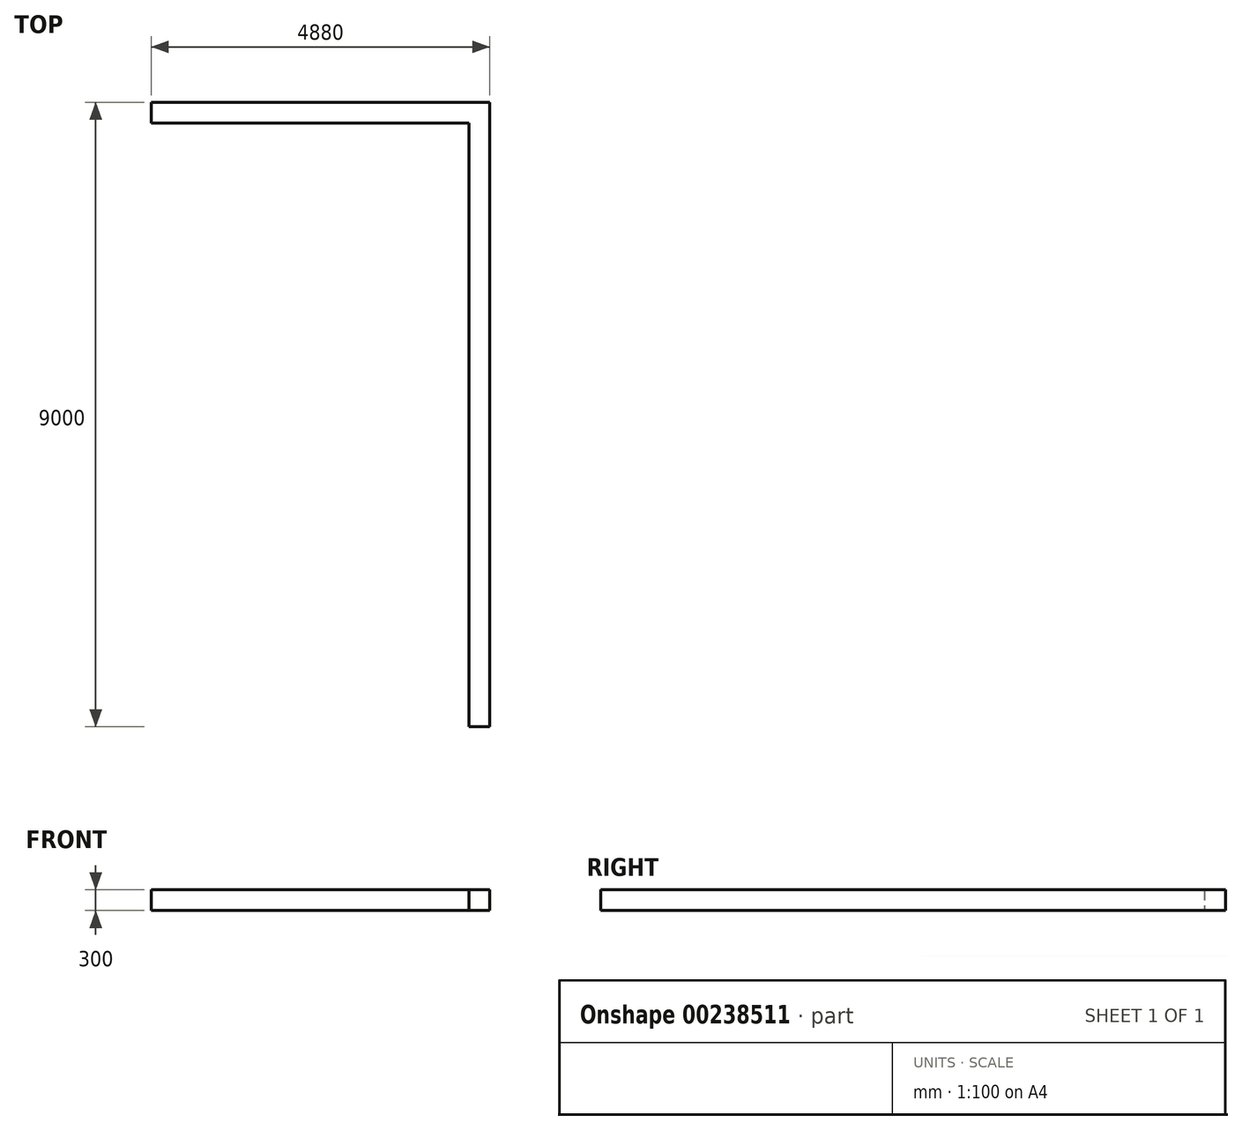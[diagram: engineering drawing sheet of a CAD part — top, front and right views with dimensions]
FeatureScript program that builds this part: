
annotation { "Feature Type Name" : "Feature", "Feature Type Description" : "" }
export const myFeature = defineFeature(function(context is Context, id is Id, definition is map)
    precondition{}
    {
        {
            var Q0;
            Q0=qCreatedBy(makeId("Top.planeOp"),FACE);
            var sketch = newSketch(context, id + "F0", { "sketchPlane" : qUnion([Q0])});
            skLineSegment(sketch, "E0", {"start": v(0, 0) * mm, "end": v(0, 9000) * mm});
            skLineSegment(sketch, "E1", {"start": v(0, 9000) * mm, "end": v(-4880, 9000) * mm});
            skLineSegment(sketch, "E2", {"start": v(-4880, 9000) * mm, "end": v(-4880, 3900) * mm});
            skLineSegment(sketch, "E3", {"start": v(-4880, 3900) * mm, "end": v(-6280, 3900) * mm});
            skLineSegment(sketch, "E4", {"start": v(-6280, 3900) * mm, "end": v(-6280, 0) * mm});
            skLineSegment(sketch, "E5", {"start": v(-6280, 0) * mm, "end": v(0, 0) * mm});
            skLineSegment(sketch, "E6", {"start": v(-4880, 8700) * mm, "end": v(-300, 8700) * mm, "construction": true});
            skLineSegment(sketch, "E7", {"start": v(-300, 8700) * mm, "end": v(-300, 0) * mm, "construction": true});
            skLineSegment(sketch, "E8", {"start": v(-4880, 5841.45) * mm, "end": v(-3164.99, 5841.45) * mm});
            skLineSegment(sketch, "E9", {"start": v(0, 5841.45) * mm, "end": v(-2221.97, 5841.45) * mm});
            skLineSegment(sketch, "E10", {"start": v(-2221.97, 5841.45) * mm, "end": v(-2709.05, 5354.37) * mm});
            skSolve(sketch);
        }
        {
            var Q0;
            Q0=qCreatedBy(makeId("Top.planeOp"),FACE);
            var sketch = newSketch(context, id + "F1", { "sketchPlane" : qUnion([Q0])});
            skLineSegment(sketch, "E11", {"start": v(0, 0) * mm, "end": v(0, 9000) * mm});
            skLineSegment(sketch, "E12", {"start": v(0, 9000) * mm, "end": v(-4880, 9000) * mm});
            skLineSegment(sketch, "E13", {"start": v(-4880, 8700) * mm, "end": v(-300, 8700) * mm});
            skLineSegment(sketch, "E14", {"start": v(-300, 8700) * mm, "end": v(-300, 0) * mm});
            skLineSegment(sketch, "E15", {"start": v(-4880, 9000) * mm, "end": v(-4880, 8700) * mm});
            skLineSegment(sketch, "E16", {"start": v(-300, 0) * mm, "end": v(0, 0) * mm});
            skSolve(sketch);
        }
        {
            var Q0;
            Q0 = qSketchRegion(id + "F1", true);
            extrude(context, id + "F2", {"entities" : qUnion([Q0]), "depth" : 300 * mm});
        }
    });
